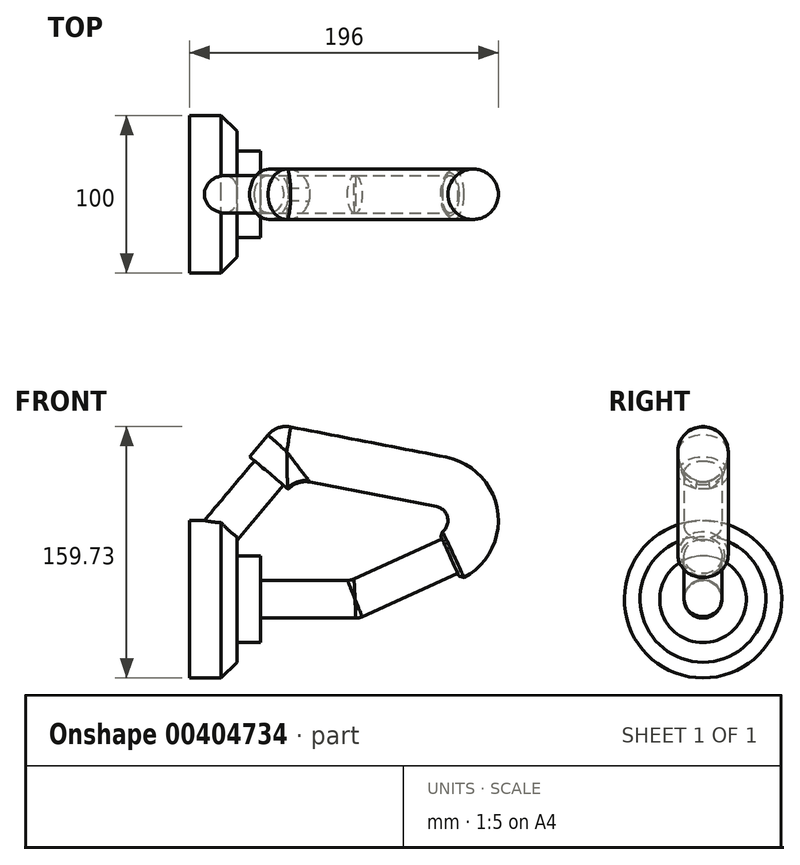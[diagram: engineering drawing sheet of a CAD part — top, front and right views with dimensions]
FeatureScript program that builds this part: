
annotation { "Feature Type Name" : "Feature", "Feature Type Description" : "" }
export const myFeature = defineFeature(function(context is Context, id is Id, definition is map)
    precondition{}
    {
        {
            var Q0;
            Q0=qCreatedBy(makeId("Front.planeOp"),FACE);
            var sketch = newSketch(context, id + "F0", { "sketchPlane" : qUnion([Q0])});
            skLineSegment(sketch, "E0", {"start": v(0, 0) * mm, "end": v(80, 0) * mm});
            skLineSegment(sketch, "E1", {"start": v(80, 0) * mm, "end": v(140.29, 27.21) * mm});
            skLineSegment(sketch, "E2", {"start": v(134.77, 74.54) * mm, "end": v(36.61, 93.63) * mm});
            skLineSegment(sketch, "E3", {"start": v(36.61, 93.63) * mm, "end": v(0, 50) * mm});
            skArc(sketch, "E4.filletArc", {"start": v(140.29, 27.21) * mm, "mid": v(154.83, 52.9) * mm, "end": v(134.77, 74.54) * mm});
            skLineSegment(sketch, "E5", {"start": v(0, 50) * mm, "end": v(-10, 38.08) * mm});
            skSolve(sketch);
        }
        {
            var Q0;
            Q0=qCreatedBy(makeId("Right.planeOp"),FACE);
            var sketch = newSketch(context, id + "F1", { "sketchPlane" : qUnion([Q0])});
            skCircle(sketch, "E6", {"center": v(0, 0) * mm, "radius": 16 * mm});
            skSolve(sketch);
        }
        {
            var Q0;
            Q0=qSketchRegion(id+"F1",true);
            var Q1;
            Q1=qConstructionFilter(qBodyType(qCreatedBy(id+"F0",EDGE),BodyType.WIRE),ConstructionObject.NO);
            sweep(context, id + "F2", {"profiles" : qUnion([Q0]), "path" : qUnion([Q1])});
        }
        {
            var Q0;
            Q0=makeQuery(id+"F2.opSweep","CAP_FACE",FACE,{"disambiguationData":[OSD([sQuery(id+"F0.wireOp",VERTEX,"E0.start"),sQuery(id+"F1.wireOp",EDGE,"E6")])],"isStart":true});
            var sketch = newSketch(context, id + "F3", { "sketchPlane" : qUnion([Q0])});
            skCircle(sketch, "E7", {"center": v(0, 0) * mm, "radius": 12 * mm});
            skSolve(sketch);
        }
        {
            var Q0;
            Q0=makeQuery(id+"F3.imprint","IMPRINT",FACE,{"disambiguationData":[TD([[makeQuery(id+"F3.imprint","IMPRINT",EDGE,{"derivedFrom":sQuery(id+"F3.wireOp",EDGE,"E7")}),-1.0]])]});
            var Q1;
            Q1=sQuery(id+"F0.wireOp",EDGE,"E0");
            var Q2;
            Q2=sQuery(id+"F0.wireOp",EDGE,"E1");
            sweep(context, id + "F4", {"operationType" : NewBodyOperationType.REMOVE, "profiles" : qUnion([Q0]), "path" : qUnion([Q1, Q2])});
        }
        {
            var Q0;
            Q0=makeQuery(id+"F2.opSweep","CAP_FACE",FACE,{"disambiguationData":[OSD([sQuery(id+"F0.wireOp",VERTEX,"E5.end"),sQuery(id+"F1.wireOp",EDGE,"E6")])],"isStart":false});
            var sketch = newSketch(context, id + "F5", { "sketchPlane" : qUnion([Q0])});
            skCircle(sketch, "E8", {"center": v(-32.14, 0) * mm, "radius": 12 * mm});
            skSolve(sketch);
        }
        {
            var Q0;
            Q0=makeQuery(id+"F5.imprint","IMPRINT",FACE,{"disambiguationData":[TD([[makeQuery(id+"F5.imprint","IMPRINT",EDGE,{"derivedFrom":sQuery(id+"F5.wireOp",EDGE,"E8")}),-1.0]])]});
            extrude(context, id + "F6", {"entities" : qUnion([Q0]), "operationType" : NewBodyOperationType.REMOVE, "oppositeDirection" : true, "depth" : 55 * mm});
        }
        {
            var Q0;
            Q0=makeQuery(id+"F2.opSweep","MID_CAP_EDGE",EDGE,{"disambiguationData":[OSD([sQuery(id+"F0.wireOp",VERTEX,"E3.start"),sQuery(id+"F1.wireOp",EDGE,"E6")])],"capPos":4.0});
            var Q1;
            Q1=makeQuery(id+"F2.opSweep","MID_CAP_EDGE",EDGE,{"disambiguationData":[OSD([sQuery(id+"F0.wireOp",VERTEX,"E1.start"),sQuery(id+"F1.wireOp",EDGE,"E6")])],"capPos":1.0});
            fillet(context, id + "F7", {"entities" : qUnion([Q0, Q1]), "radius" : 15 * mm, "tangentPropagation" : true, "allowEdgeOverflow" : false});
        }
        {
            var Q0;
            Q0=makeQuery(id+"F4.boolean.opBoolean","COPY",EDGE,{"derivedFrom":makeQuery(id+"F4.opSweep","MID_CAP_EDGE",EDGE,{"disambiguationData":[OSD([sQuery(id+"F0.wireOp",VERTEX,"E1.start"),sQuery(id+"F3.wireOp",EDGE,"E7")])],"capPos":1.0})});
            fillet(context, id + "F8", {"entities" : qUnion([Q0]), "radius" : 10 * mm, "tangentPropagation" : true, "allowEdgeOverflow" : false});
        }
        {
            var Q0;
            Q0=makeQuery(id+"F6.boolean.opBoolean","COPY",EDGE,{"derivedFrom":makeQuery(id+"F6.opExtrude","CAP_EDGE",EDGE,{"disambiguationData":[OSD([sQuery(id+"F0.wireOp",VERTEX,"E5.end"),sQuery(id+"F1.wireOp",EDGE,"E6")])],"isStart":false})});
            var Q1;
            {var subQ0=sQuery(id+"F1.wireOp",EDGE,"E6");Q1=makeQuery(id+"F4.boolean.opBoolean","MERGE",EDGE,{"derivedFrom":[makeQuery(id+"F2.opSweep","MID_CAP_EDGE",EDGE,{"disambiguationData":[OSD([sQuery(id+"F0.wireOp",VERTEX,"E4.filletArc.start"),subQ0])],"capPos":2.0}),makeQuery(id+"F4.opSweep","CAP_EDGE",EDGE,{"disambiguationData":[OSD([sQuery(id+"F0.wireOp",VERTEX,"E0.start"),sQuery(id+"F0.wireOp",VERTEX,"E1.end"),subQ0])],"isStart":false})]});}
            chamfer(context, id + "F9", {"entities" : qUnion([Q0, Q1]), "width" : 2 * mm, "tangentPropagation" : true});
        }
        {
            var Q0;
            Q0=qCreatedBy(makeId("Right.planeOp"),FACE);
            var sketch = newSketch(context, id + "F10", { "sketchPlane" : qUnion([Q0])});
            skCircle(sketch, "E9", {"center": v(0, 0) * mm, "radius": 50 * mm});
            skCircle(sketch, "E10", {"center": v(0, 0) * mm, "radius": 27.5 * mm});
            skSolve(sketch);
        }
        {
            var Q0;
            Q0=makeQuery(id+"F10.imprint","IMPRINT",FACE,{"disambiguationData":[TD([[makeQuery(id+"F10.imprint","IMPRINT",EDGE,{"derivedFrom":sQuery(id+"F10.wireOp",EDGE,"E9")}),1.0]])]});
            var Q1;
            Q1=makeQuery(id+"F10.imprint","IMPRINT",FACE,{"disambiguationData":[TD([[makeQuery(id+"F10.imprint","IMPRINT",EDGE,{"derivedFrom":sQuery(id+"F10.wireOp",EDGE,"E10")}),1.0]])]});
            var Q2;
            Q2=makeQuery(id+"F2.opSweep","SWEPT_FACE",FACE,{"disambiguationData":[OSD([sQuery(id+"F0.wireOp",EDGE,"fqPASqsh-2ivM-S5vX-Chw3-lltX0I7SKHM3"),sQuery(id+"F1.wireOp",EDGE,"1e2fa84c-9f14-412e-805f-8fcdc3764eb5.3")])]});
            extrude(context, id + "F11", {"entities" : qUnion([Q0, Q1]), "operationType" : NewBodyOperationType.ADD, "oppositeDirection" : true, "endBoundEntityFace" : qUnion([Q2]), "depth" : 25 * mm, "hasSecondDirection" : true, "secondDirectionOppositeDirection" : false, "secondDirectionDepth" : 5 * mm});
        }
        {
            var Q0;
            Q0=makeQuery(id+"F11.opExtrude","CAP_EDGE",EDGE,{"disambiguationData":[OSD([sQuery(id+"F10.wireOp",EDGE,"E9")])],"isStart":true});
            chamfer(context, id + "F12", {"entities" : qUnion([Q0]), "width" : 10 * mm, "tangentPropagation" : true});
        }
        {
            var Q0;
            Q0=makeQuery(id+"F10.imprint","IMPRINT",FACE,{"disambiguationData":[TD([[makeQuery(id+"F10.imprint","IMPRINT",EDGE,{"derivedFrom":sQuery(id+"F10.wireOp",EDGE,"E10")}),1.0]])]});
            extrude(context, id + "F13", {"entities" : qUnion([Q0]), "operationType" : NewBodyOperationType.ADD, "depth" : 20 * mm});
        }
    });
